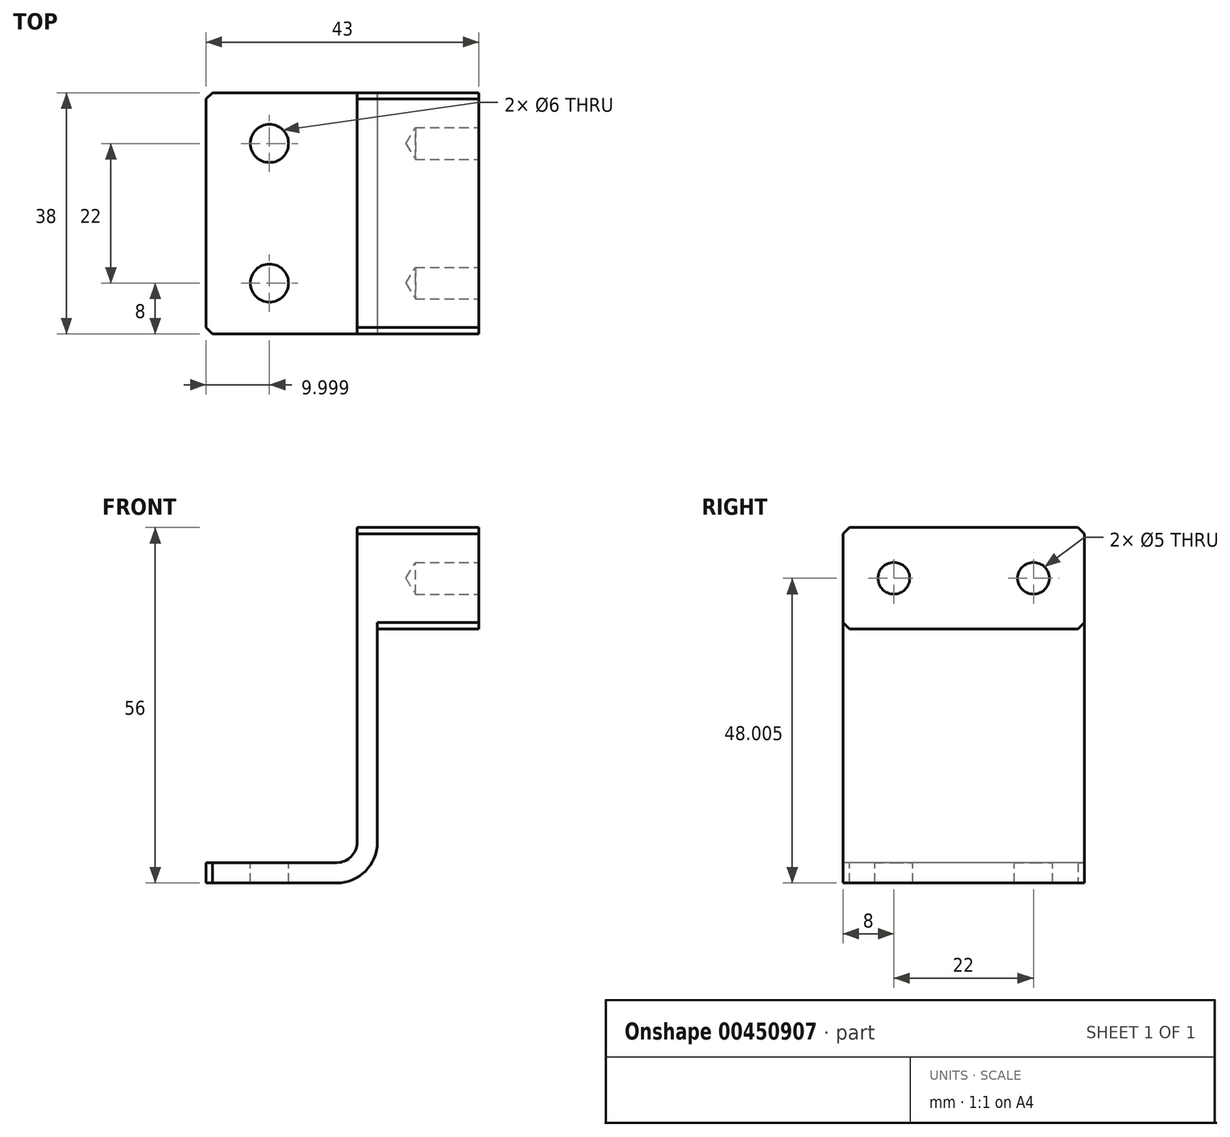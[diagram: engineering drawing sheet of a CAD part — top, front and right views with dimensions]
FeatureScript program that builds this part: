
annotation { "Feature Type Name" : "Feature", "Feature Type Description" : "" }
export const myFeature = defineFeature(function(context is Context, id is Id, definition is map)
    precondition{}
    {
        {
            var Q0;
            Q0=qCreatedBy(makeId("Front.planeOp"),FACE);
            var sketch = newSketch(context, id + "F0", { "sketchPlane" : qUnion([Q0])});
            skLineSegment(sketch, "E0", {"start": v(193.76, -142.42) * mm, "end": v(193.76, -92.82) * mm});
            skArc(sketch, "E1", {"start": v(187.36, -148.82) * mm, "mid": v(191.88, -146.94) * mm, "end": v(193.76, -142.42) * mm});
            skLineSegment(sketch, "E2", {"start": v(190.56, -142.42) * mm, "end": v(190.56, -92.82) * mm});
            skArc(sketch, "E3", {"start": v(187.36, -145.62) * mm, "mid": v(189.62, -144.68) * mm, "end": v(190.56, -142.42) * mm});
            skLineSegment(sketch, "E4", {"start": v(209.76, -108.82) * mm, "end": v(193.76, -108.82) * mm});
            skLineSegment(sketch, "E5", {"start": v(209.76, -92.82) * mm, "end": v(193.76, -92.82) * mm});
            skLineSegment(sketch, "E6", {"start": v(187.36, -148.82) * mm, "end": v(166.76, -148.82) * mm});
            skLineSegment(sketch, "E7", {"start": v(187.36, -145.62) * mm, "end": v(166.76, -145.62) * mm});
            skLineSegment(sketch, "E8", {"start": v(166.76, -148.82) * mm, "end": v(166.76, -145.62) * mm});
            skLineSegment(sketch, "E9", {"start": v(209.76, -108.82) * mm, "end": v(209.76, -92.82) * mm});
            skLineSegment(sketch, "E10", {"start": v(310.4, -145.62) * mm, "end": v(272.4, -145.62) * mm});
            skLineSegment(sketch, "E11", {"start": v(310.4, -148.82) * mm, "end": v(272.4, -148.82) * mm});
            skLineSegment(sketch, "E12", {"start": v(309.4, -92.82) * mm, "end": v(273.4, -92.82) * mm});
            skLineSegment(sketch, "E13", {"start": v(310.4, -148.82) * mm, "end": v(310.4, -93.82) * mm});
            skLineSegment(sketch, "E14", {"start": v(272.4, -148.82) * mm, "end": v(272.4, -93.82) * mm});
            skLineSegment(sketch, "E15", {"start": v(309.4, -108.82) * mm, "end": v(273.4, -108.82) * mm});
            skLineSegment(sketch, "E16", {"start": v(166.76, -54.86) * mm, "end": v(166.76, -18.86) * mm});
            skLineSegment(sketch, "E17", {"start": v(193.76, -55.86) * mm, "end": v(193.76, -17.86) * mm});
            skLineSegment(sketch, "E18", {"start": v(167.76, -55.86) * mm, "end": v(193.76, -55.86) * mm});
            skLineSegment(sketch, "E19", {"start": v(167.76, -17.86) * mm, "end": v(193.76, -17.86) * mm});
            skLineSegment(sketch, "E20", {"start": v(193.76, -55.86) * mm, "end": v(209.76, -55.86) * mm});
            skLineSegment(sketch, "E21", {"start": v(193.76, -17.86) * mm, "end": v(209.76, -17.86) * mm});
            skLineSegment(sketch, "E22", {"start": v(193.76, -17.86) * mm, "end": v(193.76, -55.86) * mm});
            skLineSegment(sketch, "E23", {"start": v(190.56, -17.86) * mm, "end": v(190.56, -55.86) * mm});
            skLineSegment(sketch, "E24", {"start": v(209.76, -17.86) * mm, "end": v(209.76, -55.86) * mm});
            skLineSegment(sketch, "E25", {"start": v(280.4, -97.07) * mm, "end": v(280.4, -104.57) * mm});
            skCircle(sketch, "E26", {"center": v(280.4, -100.82) * mm, "radius": 2.07 * mm});
            skCircle(sketch, "E27", {"center": v(280.4, -100.82) * mm, "radius": 2.5 * mm});
            skLineSegment(sketch, "E28", {"start": v(276.65, -100.82) * mm, "end": v(284.15, -100.82) * mm});
            skLineSegment(sketch, "E29", {"start": v(302.4, -97.07) * mm, "end": v(302.4, -104.57) * mm});
            skCircle(sketch, "E30", {"center": v(302.4, -100.82) * mm, "radius": 2.07 * mm});
            skCircle(sketch, "E31", {"center": v(302.4, -100.82) * mm, "radius": 2.5 * mm});
            skLineSegment(sketch, "E32", {"start": v(298.65, -100.82) * mm, "end": v(306.15, -100.82) * mm});
            skCircle(sketch, "E33", {"center": v(176.76, -47.86) * mm, "radius": 3 * mm});
            skCircle(sketch, "E34", {"center": v(176.76, -25.86) * mm, "radius": 3 * mm});
            skLineSegment(sketch, "E35", {"start": v(176.76, -21.96) * mm, "end": v(176.76, -29.76) * mm});
            skLineSegment(sketch, "E36", {"start": v(180.66, -25.86) * mm, "end": v(172.86, -25.86) * mm});
            skLineSegment(sketch, "E37", {"start": v(176.76, -43.96) * mm, "end": v(176.76, -51.76) * mm});
            skLineSegment(sketch, "E38", {"start": v(180.66, -47.86) * mm, "end": v(172.86, -47.86) * mm});
            skLineSegment(sketch, "E39", {"start": v(193.76, -92.82) * mm, "end": v(190.56, -92.82) * mm});
            skLineSegment(sketch, "E40", {"start": v(167.76, -17.86) * mm, "end": v(166.76, -18.86) * mm});
            skLineSegment(sketch, "E41", {"start": v(167.76, -55.86) * mm, "end": v(166.76, -54.86) * mm});
            skLineSegment(sketch, "E42", {"start": v(310.4, -93.82) * mm, "end": v(309.4, -92.82) * mm});
            skLineSegment(sketch, "E43", {"start": v(273.4, -92.82) * mm, "end": v(272.4, -93.82) * mm});
            skLineSegment(sketch, "E44", {"start": v(309.4, -108.82) * mm, "end": v(310.4, -107.82) * mm});
            skLineSegment(sketch, "E45", {"start": v(273.4, -108.82) * mm, "end": v(272.4, -107.82) * mm});
            skSolve(sketch);
        }
        {
            var Q0;
            {var subQ0=sQuery(id+"F0.wireOp",EDGE,"E1");Q0=makeQuery(id+"F0.imprint","IMPRINT",FACE,{"disambiguationData":[TD([[makeQuery(id+"F0.imprint","IMPRINT",EDGE,{"derivedFrom":subQ0}),1.0]])]});}
            extrude(context, id + "F1", {"entities" : qUnion([Q0]), "depth" : -38 * mm});
        }
        {
            var Q0;
            {var subQ2=sQuery(id+"F0.wireOp",EDGE,"E4");Q0=makeQuery(id+"F0.imprint","IMPRINT",FACE,{"disambiguationData":[TD([[makeQuery(id+"F0.imprint","IMPRINT",EDGE,{"derivedFrom":subQ2}),-1.0]])]});}
            extrude(context, id + "F2", {"entities" : qUnion([Q0]), "operationType" : NewBodyOperationType.ADD, "depth" : -38 * mm});
        }
        {
            var Q0;
            Q0=makeQuery(id+"F2.opExtrude","SWEPT_FACE",FACE,{"disambiguationData":[OSD([sQuery(id+"F0.wireOp",EDGE,"E9")])]});
            var sketch = newSketch(context, id + "F3", { "sketchPlane" : qUnion([Q0])});
            skLineSegment(sketch, "E46.0", {"start": v(8, -108.82) * mm, "end": v(8, -92.82) * mm});
            skLineSegment(sketch, "E47.0", {"start": v(30, -108.82) * mm, "end": v(30, -92.82) * mm});
            skLineSegment(sketch, "E48.0", {"start": v(38, -100.82) * mm, "end": v(0, -100.82) * mm});
            skLineSegment(sketch, "E49.0", {"start": v(5, -97.82) * mm, "end": v(5, -103.82) * mm});
            skLineSegment(sketch, "E49.1", {"start": v(33, -97.82) * mm, "end": v(5, -97.82) * mm});
            skLineSegment(sketch, "E49.2", {"start": v(33, -103.82) * mm, "end": v(33, -97.82) * mm});
            skLineSegment(sketch, "E49.3", {"start": v(5, -103.82) * mm, "end": v(33, -103.82) * mm});
            skPoint(sketch, "E50", {"position": v(8, -100.82) * mm});
            skPoint(sketch, "E51", {"position": v(30, -100.82) * mm});
            skSolve(sketch);
        }
        {
            var Q0;
            Q0=sQuery(id+"F3.wireOp",VERTEX,"E50");
            var Q1;
            Q1=sQuery(id+"F3.wireOp",VERTEX,"E51");
            var Q2;
            Q2=makeQuery(id+"F1.opExtrude","SWEPT_BODY",BODY,{"disambiguationData":[OSD([sQuery(id+"F0.wireOp",EDGE,"E0"),sQuery(id+"F0.wireOp",EDGE,"E1"),sQuery(id+"F0.wireOp",EDGE,"E2"),sQuery(id+"F0.wireOp",EDGE,"E3"),sQuery(id+"F0.wireOp",EDGE,"E6"),sQuery(id+"F0.wireOp",EDGE,"E7"),sQuery(id+"F0.wireOp",EDGE,"E8"),sQuery(id+"F0.wireOp",EDGE,"E39")])]});
            hole(context, id + "F4", {"style" : HoleStyle.SIMPLE, "endStyle" : HoleEndStyle.BLIND, "holeDiameter" : 5 * mm, "holeDepth" : 10 * mm, "isTappedThrough" : true, "tappedDepth" : 12 * mm, "tapClearance" : 3, "locations" : qUnion([Q0, Q1]), "scope" : qUnion([Q2])});
        }
        {
            var Q0;
            Q0=makeQuery(id+"F1.opExtrude","SWEPT_FACE",FACE,{"disambiguationData":[OSD([sQuery(id+"F0.wireOp",EDGE,"E7")])]});
            var sketch = newSketch(context, id + "F5", { "sketchPlane" : qUnion([Q0])});
            skLineSegment(sketch, "E52.0", {"start": v(187.36, 8) * mm, "end": v(166.76, 8) * mm});
            skLineSegment(sketch, "E53.0", {"start": v(187.36, 30) * mm, "end": v(166.76, 30) * mm});
            skLineSegment(sketch, "E54.0", {"start": v(176.76, 38) * mm, "end": v(176.76, 0) * mm});
            skPoint(sketch, "E55", {"position": v(176.76, 30) * mm});
            skPoint(sketch, "E56", {"position": v(176.76, 8) * mm});
            skSolve(sketch);
        }
        {
            var Q0;
            Q0=sQuery(id+"F5.wireOp",VERTEX,"E55");
            var Q1;
            Q1=sQuery(id+"F5.wireOp",VERTEX,"E56");
            var Q2;
            Q2=makeQuery(id+"F1.opExtrude","SWEPT_BODY",BODY,{"disambiguationData":[OSD([sQuery(id+"F0.wireOp",EDGE,"E0"),sQuery(id+"F0.wireOp",EDGE,"E1"),sQuery(id+"F0.wireOp",EDGE,"E2"),sQuery(id+"F0.wireOp",EDGE,"E3"),sQuery(id+"F0.wireOp",EDGE,"E6"),sQuery(id+"F0.wireOp",EDGE,"E7"),sQuery(id+"F0.wireOp",EDGE,"E8"),sQuery(id+"F0.wireOp",EDGE,"E39")])]});
            hole(context, id + "F6", {"style" : HoleStyle.SIMPLE, "endStyle" : HoleEndStyle.THROUGH, "holeDiameter" : 6 * mm, "isTappedThrough" : true, "tappedDepth" : 12 * mm, "tapClearance" : 3, "locations" : qUnion([Q0, Q1]), "scope" : qUnion([Q2])});
        }
        {
            var Q0;
            Q0=makeQuery(id+"F1.opExtrude","CAP_EDGE",EDGE,{"disambiguationData":[OSD([sQuery(id+"F0.wireOp",EDGE,"E8")])],"isStart":true});
            var Q1;
            Q1=makeQuery(id+"F1.opExtrude","CAP_EDGE",EDGE,{"disambiguationData":[OSD([sQuery(id+"F0.wireOp",EDGE,"E8")])],"isStart":false});
            chamfer(context, id + "F7", {"entities" : qUnion([Q0, Q1]), "width" : 1 * mm, "tangentPropagation" : true});
        }
        {
            var Q0;
            Q0=makeQuery(id+"F2.boolean.opBoolean","MERGE",EDGE,{"derivedFrom":[makeQuery(id+"F1.opExtrude","CAP_EDGE",EDGE,{"disambiguationData":[OSD([sQuery(id+"F0.wireOp",EDGE,"E39")])],"isStart":true}),makeQuery(id+"F2.opExtrude","CAP_EDGE",EDGE,{"disambiguationData":[OSD([sQuery(id+"F0.wireOp",EDGE,"E5")])],"isStart":true})]});
            var Q1;
            Q1=makeQuery(id+"F2.boolean.opBoolean","MERGE",EDGE,{"derivedFrom":[makeQuery(id+"F1.opExtrude","CAP_EDGE",EDGE,{"disambiguationData":[OSD([sQuery(id+"F0.wireOp",EDGE,"E39")])],"isStart":false}),makeQuery(id+"F2.opExtrude","CAP_EDGE",EDGE,{"disambiguationData":[OSD([sQuery(id+"F0.wireOp",EDGE,"E5")])],"isStart":false})]});
            var Q2;
            Q2=makeQuery(id+"F2.opExtrude","CAP_EDGE",EDGE,{"disambiguationData":[OSD([sQuery(id+"F0.wireOp",EDGE,"E4")])],"isStart":false});
            var Q3;
            Q3=makeQuery(id+"F2.opExtrude","CAP_EDGE",EDGE,{"disambiguationData":[OSD([sQuery(id+"F0.wireOp",EDGE,"E4")])],"isStart":true});
            chamfer(context, id + "F8", {"entities" : qUnion([Q0, Q1, Q2, Q3]), "width" : 1 * mm, "tangentPropagation" : true});
        }
    });
